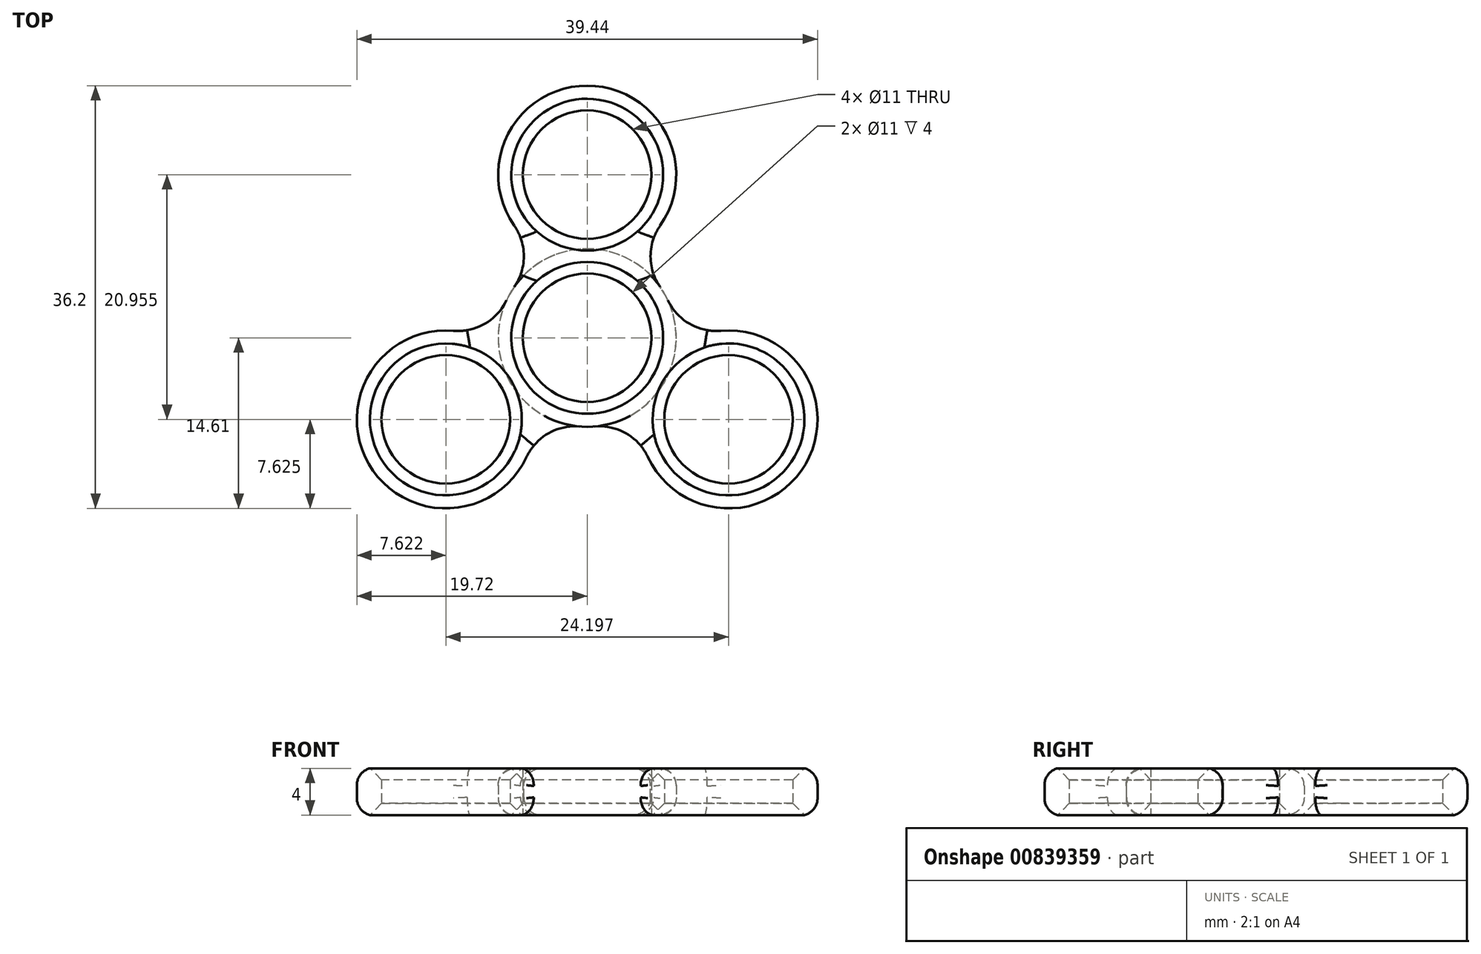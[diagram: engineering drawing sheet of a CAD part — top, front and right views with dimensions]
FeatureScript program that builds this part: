
annotation { "Feature Type Name" : "Feature", "Feature Type Description" : "" }
export const myFeature = defineFeature(function(context is Context, id is Id, definition is map)
    precondition{}
    {
        {
            var Q0;
            Q0=qCreatedBy(makeId("Top.planeOp"),FACE);
            var sketch = newSketch(context, id + "F0", { "sketchPlane" : qUnion([Q0])});
            skCircle(sketch, "E0", {"center": v(0, 0) * mm, "radius": 5.5 * mm});
            skCircle(sketch, "E1.cCircle", {"center": v(0, 13.97) * mm, "radius": 5.5 * mm});
            skCircle(sketch, "E2", {"center": v(0, 13.97) * mm, "radius": 7.62 * mm});
            skCircle(sketch, "E3", {"center": v(0, 0) * mm, "radius": 7.62 * mm});
            skSolve(sketch);
        }
        {
            var Q0;
            Q0=makeQuery(id+"F0.imprint","IMPRINT",FACE,{"disambiguationData":[TD([[makeQuery(id+"F0.imprint","IMPRINT",EDGE,{"derivedFrom":sQuery(id+"F0.wireOp",EDGE,"E0")}),-1.0]])]});
            var Q1;
            Q1=makeQuery(id+"F0.imprint","IMPRINT",FACE,{"disambiguationData":[TD([[makeQuery(id+"F0.imprint","IMPRINT",EDGE,{"derivedFrom":sQuery(id+"F0.wireOp",EDGE,"E1.cCircle")}),-1.0]])]});
            var Q2;
            {var subQ0=sQuery(id+"F0.wireOp",EDGE,"E3");var subQ1=sQuery(id+"F0.wireOp",EDGE,"E2");var subQ2=makeQuery(id+"F0.imprint","INTERSECT",VERTEX,{"disambiguationData":[OD(0.0)],"derivedFrom":[subQ1,subQ0]});Q2=makeQuery(id+"F0.imprint","IMPRINT",FACE,{"disambiguationData":[TD([[makeQuery(id+"F0.imprint","IMPRINT",EDGE,{"disambiguationData":[TD([[subQ2,-1.0]])],"derivedFrom":subQ1}),1.0]])]});}
            extrude(context, id + "F1", {"entities" : qUnion([Q0, Q1, Q2]), "depth" : 4 * mm, "offsetDistance" : 25.4 * mm});
        }
        {
            var Q0;
            {var subQ0=sQuery(id+"F0.wireOp",EDGE,"E3");var subQ1=sQuery(id+"F0.wireOp",EDGE,"E2");Q0=makeQuery(id+"F1.opExtrude","SWEPT_EDGE",EDGE,{"disambiguationData":[OSD([subQ1,subQ0]),TDD([makeQuery(id+"F0.imprint","INTERSECT",VERTEX,{"disambiguationData":[OD(0.0)],"derivedFrom":[subQ1,subQ0]})])]});}
            var Q1;
            {var subQ0=sQuery(id+"F0.wireOp",EDGE,"E3");var subQ1=sQuery(id+"F0.wireOp",EDGE,"E2");Q1=makeQuery(id+"F1.opExtrude","SWEPT_EDGE",EDGE,{"disambiguationData":[OSD([subQ1,subQ0]),TDD([makeQuery(id+"F0.imprint","INTERSECT",VERTEX,{"disambiguationData":[OD(1.0)],"derivedFrom":[subQ1,subQ0]})])]});}
            fillet(context, id + "F2", {"entities" : qUnion([Q0, Q1]), "radius" : 4.57 * mm, "tangentPropagation" : true, "allowEdgeOverflow" : false});
        }
        {
            var Q0;
            Q0=makeQuery(id+"F1.opExtrude","SWEPT_BODY",BODY,{"disambiguationData":[OSD([sQuery(id+"F0.wireOp",EDGE,"E0"),sQuery(id+"F0.wireOp",EDGE,"d1f96c89-ae24-44dc-95b8-3d53eee9b90a.0"),sQuery(id+"F0.wireOp",EDGE,"E1.0"),sQuery(id+"F0.wireOp",EDGE,"E1.1"),sQuery(id+"F0.wireOp",EDGE,"E1.2"),sQuery(id+"F0.wireOp",EDGE,"E1.3"),sQuery(id+"F0.wireOp",EDGE,"E1.4"),sQuery(id+"F0.wireOp",EDGE,"E1.5"),sQuery(id+"F0.wireOp",EDGE,"6467eb64-f5fc-4fa4-b67a-5fdd80484858.0"),sQuery(id+"F0.wireOp",EDGE,"6467eb64-f5fc-4fa4-b67a-5fdd80484858.2"),sQuery(id+"F0.wireOp",EDGE,"6467eb64-f5fc-4fa4-b67a-5fdd80484858.3"),sQuery(id+"F0.wireOp",EDGE,"6467eb64-f5fc-4fa4-b67a-5fdd80484858.4"),sQuery(id+"F0.wireOp",EDGE,"6467eb64-f5fc-4fa4-b67a-5fdd80484858.5"),sQuery(id+"F0.wireOp",EDGE,"e1e534cc-2f33-4b0f-82cc-b4de4e4070e7"),sQuery(id+"F0.wireOp",EDGE,"d04765f5-1735-495e-b364-6d969f9b3d5d"),sQuery(id+"F0.wireOp",EDGE,"77a682f6-1ae9-43b9-b4da-7f019d4a444a.0"),sQuery(id+"F0.wireOp",EDGE,"27ab2300-1543-4c0a-a06e-bdf80a921956.0"),sQuery(id+"F0.wireOp",EDGE,"7b8874fc-19ec-4d05-a443-a3cdac1f19cd.filletArc"),sQuery(id+"F0.wireOp",EDGE,"lxG7lnsp-9xvN-WL6z-RJoO-r6IwSvIQtlOm"),sQuery(id+"F0.wireOp",EDGE,"8nAJOfJ4-Ij3l-DfIw-Xt9b-HZkO6DjjanfU")])]});
            var Q1;
            Q1=makeQuery(id+"F1.opExtrude","SWEPT_FACE",FACE,{"disambiguationData":[OSD([sQuery(id+"F0.wireOp",EDGE,"E0")])]});
            circularPattern(context, id + "F3", {"entities" : qUnion([Q0]), "axis" : qUnion([Q1]), "angle" : 360 * degree, "instanceCount" : 3, "oppositeDirection" : true, "equalSpace" : true});
        }
        {
            var Q0;
            Q0=makeQuery(id+"F1.opExtrude","SWEPT_FACE",FACE,{"disambiguationData":[OSD([sQuery(id+"F0.wireOp",EDGE,"E0")])]});
            var Q1;
            Q1=makeQuery(id+"F3.opPattern","COPY",EDGE,{"derivedFrom":makeQuery(id+"F1.opExtrude","CAP_EDGE",EDGE,{"disambiguationData":[OSD([sQuery(id+"F0.wireOp",EDGE,"E1.3")])],"isStart":true}),"instanceName":"1"});
            var Q2;
            Q2=makeQuery(id+"F3.opPattern","COPY",EDGE,{"derivedFrom":makeQuery(id+"F1.opExtrude","CAP_EDGE",EDGE,{"disambiguationData":[OSD([sQuery(id+"F0.wireOp",EDGE,"E1.3")])],"isStart":false}),"instanceName":"1"});
            var Q3;
            Q3=makeQuery(id+"F3.opPattern","COPY",EDGE,{"derivedFrom":makeQuery(id+"F1.opExtrude","CAP_EDGE",EDGE,{"disambiguationData":[OSD([sQuery(id+"F0.wireOp",EDGE,"E1.2")])],"isStart":false}),"instanceName":"1"});
            var Q4;
            Q4=makeQuery(id+"F3.opPattern","COPY",EDGE,{"derivedFrom":makeQuery(id+"F1.opExtrude","CAP_EDGE",EDGE,{"disambiguationData":[OSD([sQuery(id+"F0.wireOp",EDGE,"E1.2")])],"isStart":true}),"instanceName":"1"});
            var Q5;
            Q5=makeQuery(id+"F3.opPattern","COPY",EDGE,{"derivedFrom":makeQuery(id+"F1.opExtrude","CAP_EDGE",EDGE,{"disambiguationData":[OSD([sQuery(id+"F0.wireOp",EDGE,"E1.1")])],"isStart":false}),"instanceName":"1"});
            var Q6;
            Q6=makeQuery(id+"F3.opPattern","COPY",EDGE,{"derivedFrom":makeQuery(id+"F1.opExtrude","CAP_EDGE",EDGE,{"disambiguationData":[OSD([sQuery(id+"F0.wireOp",EDGE,"E1.0")])],"isStart":false}),"instanceName":"1"});
            var Q7;
            Q7=makeQuery(id+"F3.opPattern","COPY",EDGE,{"derivedFrom":makeQuery(id+"F1.opExtrude","CAP_EDGE",EDGE,{"disambiguationData":[OSD([sQuery(id+"F0.wireOp",EDGE,"E1.5")])],"isStart":false}),"instanceName":"1"});
            var Q8;
            Q8=makeQuery(id+"F3.opPattern","COPY",EDGE,{"derivedFrom":makeQuery(id+"F1.opExtrude","CAP_EDGE",EDGE,{"disambiguationData":[OSD([sQuery(id+"F0.wireOp",EDGE,"E1.4")])],"isStart":true}),"instanceName":"1"});
            var Q9;
            Q9=makeQuery(id+"F3.opPattern","COPY",EDGE,{"derivedFrom":makeQuery(id+"F1.opExtrude","CAP_EDGE",EDGE,{"disambiguationData":[OSD([sQuery(id+"F0.wireOp",EDGE,"E1.4")])],"isStart":false}),"instanceName":"1"});
            var Q10;
            Q10=makeQuery(id+"F1.opExtrude","CAP_EDGE",EDGE,{"disambiguationData":[OSD([sQuery(id+"F0.wireOp",EDGE,"E1.1")])],"isStart":false});
            var Q11;
            Q11=makeQuery(id+"F1.opExtrude","CAP_EDGE",EDGE,{"disambiguationData":[OSD([sQuery(id+"F0.wireOp",EDGE,"E1.1")])],"isStart":true});
            var Q12;
            Q12=makeQuery(id+"F1.opExtrude","CAP_EDGE",EDGE,{"disambiguationData":[OSD([sQuery(id+"F0.wireOp",EDGE,"E1.0")])],"isStart":true});
            var Q13;
            Q13=makeQuery(id+"F1.opExtrude","CAP_EDGE",EDGE,{"disambiguationData":[OSD([sQuery(id+"F0.wireOp",EDGE,"E1.0")])],"isStart":false});
            var Q14;
            Q14=makeQuery(id+"F1.opExtrude","CAP_EDGE",EDGE,{"disambiguationData":[OSD([sQuery(id+"F0.wireOp",EDGE,"E1.5")])],"isStart":false});
            var Q15;
            Q15=makeQuery(id+"F1.opExtrude","CAP_EDGE",EDGE,{"disambiguationData":[OSD([sQuery(id+"F0.wireOp",EDGE,"E1.5")])],"isStart":true});
            var Q16;
            Q16=makeQuery(id+"F1.opExtrude","CAP_EDGE",EDGE,{"disambiguationData":[OSD([sQuery(id+"F0.wireOp",EDGE,"E1.4")])],"isStart":false});
            var Q17;
            Q17=makeQuery(id+"F1.opExtrude","CAP_EDGE",EDGE,{"disambiguationData":[OSD([sQuery(id+"F0.wireOp",EDGE,"E1.3")])],"isStart":false});
            var Q18;
            Q18=makeQuery(id+"F1.opExtrude","CAP_EDGE",EDGE,{"disambiguationData":[OSD([sQuery(id+"F0.wireOp",EDGE,"E1.2")])],"isStart":false});
            var Q19;
            Q19=makeQuery(id+"F1.opExtrude","CAP_EDGE",EDGE,{"disambiguationData":[OSD([sQuery(id+"F0.wireOp",EDGE,"E1.3")])],"isStart":true});
            var Q20;
            Q20=makeQuery(id+"F1.opExtrude","CAP_EDGE",EDGE,{"disambiguationData":[OSD([sQuery(id+"F0.wireOp",EDGE,"E1.4")])],"isStart":true});
            var Q21;
            Q21=makeQuery(id+"F1.opExtrude","CAP_EDGE",EDGE,{"disambiguationData":[OSD([sQuery(id+"F0.wireOp",EDGE,"E1.2")])],"isStart":true});
            var Q22;
            Q22=makeQuery(id+"F3.opPattern","COPY",EDGE,{"derivedFrom":makeQuery(id+"F1.opExtrude","CAP_EDGE",EDGE,{"disambiguationData":[OSD([sQuery(id+"F0.wireOp",EDGE,"E1.5")])],"isStart":true}),"instanceName":"1"});
            var Q23;
            Q23=makeQuery(id+"F3.opPattern","COPY",EDGE,{"derivedFrom":makeQuery(id+"F1.opExtrude","CAP_EDGE",EDGE,{"disambiguationData":[OSD([sQuery(id+"F0.wireOp",EDGE,"E1.0")])],"isStart":true}),"instanceName":"1"});
            var Q24;
            Q24=makeQuery(id+"F3.opPattern","COPY",EDGE,{"derivedFrom":makeQuery(id+"F1.opExtrude","CAP_EDGE",EDGE,{"disambiguationData":[OSD([sQuery(id+"F0.wireOp",EDGE,"E1.1")])],"isStart":true}),"instanceName":"1"});
            var Q25;
            Q25=makeQuery(id+"F3.opPattern","COPY",EDGE,{"derivedFrom":makeQuery(id+"F1.opExtrude","CAP_EDGE",EDGE,{"disambiguationData":[OSD([sQuery(id+"F0.wireOp",EDGE,"E1.5")])],"isStart":false}),"instanceName":"2"});
            var Q26;
            Q26=makeQuery(id+"F3.opPattern","COPY",EDGE,{"derivedFrom":makeQuery(id+"F1.opExtrude","CAP_EDGE",EDGE,{"disambiguationData":[OSD([sQuery(id+"F0.wireOp",EDGE,"E1.5")])],"isStart":true}),"instanceName":"2"});
            var Q27;
            Q27=makeQuery(id+"F3.opPattern","COPY",EDGE,{"derivedFrom":makeQuery(id+"F1.opExtrude","CAP_EDGE",EDGE,{"disambiguationData":[OSD([sQuery(id+"F0.wireOp",EDGE,"E1.0")])],"isStart":false}),"instanceName":"2"});
            var Q28;
            Q28=makeQuery(id+"F3.opPattern","COPY",EDGE,{"derivedFrom":makeQuery(id+"F1.opExtrude","CAP_EDGE",EDGE,{"disambiguationData":[OSD([sQuery(id+"F0.wireOp",EDGE,"E1.0")])],"isStart":true}),"instanceName":"2"});
            var Q29;
            Q29=makeQuery(id+"F3.opPattern","COPY",EDGE,{"derivedFrom":makeQuery(id+"F1.opExtrude","CAP_EDGE",EDGE,{"disambiguationData":[OSD([sQuery(id+"F0.wireOp",EDGE,"E1.4")])],"isStart":false}),"instanceName":"2"});
            var Q30;
            Q30=makeQuery(id+"F3.opPattern","COPY",EDGE,{"derivedFrom":makeQuery(id+"F1.opExtrude","CAP_EDGE",EDGE,{"disambiguationData":[OSD([sQuery(id+"F0.wireOp",EDGE,"E1.4")])],"isStart":true}),"instanceName":"2"});
            var Q31;
            Q31=makeQuery(id+"F3.opPattern","COPY",EDGE,{"derivedFrom":makeQuery(id+"F1.opExtrude","CAP_EDGE",EDGE,{"disambiguationData":[OSD([sQuery(id+"F0.wireOp",EDGE,"E1.3")])],"isStart":true}),"instanceName":"2"});
            var Q32;
            Q32=makeQuery(id+"F3.opPattern","COPY",EDGE,{"derivedFrom":makeQuery(id+"F1.opExtrude","CAP_EDGE",EDGE,{"disambiguationData":[OSD([sQuery(id+"F0.wireOp",EDGE,"E1.2")])],"isStart":true}),"instanceName":"2"});
            var Q33;
            Q33=makeQuery(id+"F3.opPattern","COPY",EDGE,{"derivedFrom":makeQuery(id+"F1.opExtrude","CAP_EDGE",EDGE,{"disambiguationData":[OSD([sQuery(id+"F0.wireOp",EDGE,"E1.1")])],"isStart":true}),"instanceName":"2"});
            var Q34;
            Q34=makeQuery(id+"F3.opPattern","COPY",EDGE,{"derivedFrom":makeQuery(id+"F1.opExtrude","CAP_EDGE",EDGE,{"disambiguationData":[OSD([sQuery(id+"F0.wireOp",EDGE,"E1.2")])],"isStart":false}),"instanceName":"2"});
            var Q35;
            Q35=makeQuery(id+"F3.opPattern","COPY",EDGE,{"derivedFrom":makeQuery(id+"F1.opExtrude","CAP_EDGE",EDGE,{"disambiguationData":[OSD([sQuery(id+"F0.wireOp",EDGE,"E1.1")])],"isStart":false}),"instanceName":"2"});
            var Q36;
            Q36=makeQuery(id+"F3.opPattern","COPY",EDGE,{"derivedFrom":makeQuery(id+"F1.opExtrude","CAP_EDGE",EDGE,{"disambiguationData":[OSD([sQuery(id+"F0.wireOp",EDGE,"E1.3")])],"isStart":false}),"instanceName":"2"});
            var Q37;
            Q37=makeQuery(id+"F3.opPattern","COPY",EDGE,{"derivedFrom":makeQuery(id+"F1.opExtrude","CAP_EDGE",EDGE,{"disambiguationData":[OSD([sQuery(id+"F0.wireOp",EDGE,"E1.5")])],"isStart":false}),"instanceName":"3"});
            var Q38;
            Q38=makeQuery(id+"F3.opPattern","COPY",EDGE,{"derivedFrom":makeQuery(id+"F1.opExtrude","CAP_EDGE",EDGE,{"disambiguationData":[OSD([sQuery(id+"F0.wireOp",EDGE,"E1.4")])],"isStart":false}),"instanceName":"3"});
            var Q39;
            Q39=makeQuery(id+"F3.opPattern","COPY",EDGE,{"derivedFrom":makeQuery(id+"F1.opExtrude","CAP_EDGE",EDGE,{"disambiguationData":[OSD([sQuery(id+"F0.wireOp",EDGE,"E1.3")])],"isStart":false}),"instanceName":"3"});
            var Q40;
            Q40=makeQuery(id+"F3.opPattern","COPY",EDGE,{"derivedFrom":makeQuery(id+"F1.opExtrude","CAP_EDGE",EDGE,{"disambiguationData":[OSD([sQuery(id+"F0.wireOp",EDGE,"E1.2")])],"isStart":false}),"instanceName":"3"});
            var Q41;
            Q41=makeQuery(id+"F3.opPattern","COPY",EDGE,{"derivedFrom":makeQuery(id+"F1.opExtrude","CAP_EDGE",EDGE,{"disambiguationData":[OSD([sQuery(id+"F0.wireOp",EDGE,"E1.1")])],"isStart":false}),"instanceName":"3"});
            var Q42;
            Q42=makeQuery(id+"F3.opPattern","COPY",EDGE,{"derivedFrom":makeQuery(id+"F1.opExtrude","CAP_EDGE",EDGE,{"disambiguationData":[OSD([sQuery(id+"F0.wireOp",EDGE,"E1.0")])],"isStart":false}),"instanceName":"3"});
            var Q43;
            Q43=makeQuery(id+"F3.opPattern","COPY",EDGE,{"derivedFrom":makeQuery(id+"F1.opExtrude","CAP_EDGE",EDGE,{"disambiguationData":[OSD([sQuery(id+"F0.wireOp",EDGE,"E1.5")])],"isStart":true}),"instanceName":"3"});
            var Q44;
            Q44=makeQuery(id+"F3.opPattern","COPY",EDGE,{"derivedFrom":makeQuery(id+"F1.opExtrude","CAP_EDGE",EDGE,{"disambiguationData":[OSD([sQuery(id+"F0.wireOp",EDGE,"E1.4")])],"isStart":true}),"instanceName":"3"});
            var Q45;
            Q45=makeQuery(id+"F3.opPattern","COPY",EDGE,{"derivedFrom":makeQuery(id+"F1.opExtrude","CAP_EDGE",EDGE,{"disambiguationData":[OSD([sQuery(id+"F0.wireOp",EDGE,"E1.3")])],"isStart":true}),"instanceName":"3"});
            var Q46;
            Q46=makeQuery(id+"F3.opPattern","COPY",EDGE,{"derivedFrom":makeQuery(id+"F1.opExtrude","CAP_EDGE",EDGE,{"disambiguationData":[OSD([sQuery(id+"F0.wireOp",EDGE,"E1.2")])],"isStart":true}),"instanceName":"3"});
            var Q47;
            Q47=makeQuery(id+"F3.opPattern","COPY",EDGE,{"derivedFrom":makeQuery(id+"F1.opExtrude","CAP_EDGE",EDGE,{"disambiguationData":[OSD([sQuery(id+"F0.wireOp",EDGE,"E1.1")])],"isStart":true}),"instanceName":"3"});
            var Q48;
            Q48=makeQuery(id+"F3.opPattern","COPY",EDGE,{"derivedFrom":makeQuery(id+"F1.opExtrude","CAP_EDGE",EDGE,{"disambiguationData":[OSD([sQuery(id+"F0.wireOp",EDGE,"E1.0")])],"isStart":true}),"instanceName":"3"});
            var Q49;
            Q49=makeQuery(id+"F3.opPattern","COPY",EDGE,{"derivedFrom":makeQuery(id+"F1.opExtrude","CAP_EDGE",EDGE,{"disambiguationData":[OSD([sQuery(id+"F0.wireOp",EDGE,"E1.cCircle")])],"isStart":false}),"instanceName":"2"});
            var Q50;
            Q50=makeQuery(id+"F1.opExtrude","CAP_EDGE",EDGE,{"disambiguationData":[OSD([sQuery(id+"F0.wireOp",EDGE,"E1.cCircle")])],"isStart":false});
            var Q51;
            Q51=makeQuery(id+"F3.opPattern","COPY",EDGE,{"derivedFrom":makeQuery(id+"F1.opExtrude","CAP_EDGE",EDGE,{"disambiguationData":[OSD([sQuery(id+"F0.wireOp",EDGE,"E1.cCircle")])],"isStart":false}),"instanceName":"1"});
            var Q52;
            Q52=makeQuery(id+"F3.opPattern","COPY",EDGE,{"derivedFrom":makeQuery(id+"F1.opExtrude","CAP_EDGE",EDGE,{"disambiguationData":[OSD([sQuery(id+"F0.wireOp",EDGE,"E1.cCircle")])],"isStart":true}),"instanceName":"1"});
            var Q53;
            Q53=makeQuery(id+"F1.opExtrude","CAP_EDGE",EDGE,{"disambiguationData":[OSD([sQuery(id+"F0.wireOp",EDGE,"E1.cCircle")])],"isStart":true});
            var Q54;
            Q54=makeQuery(id+"F3.opPattern","COPY",EDGE,{"derivedFrom":makeQuery(id+"F1.opExtrude","CAP_EDGE",EDGE,{"disambiguationData":[OSD([sQuery(id+"F0.wireOp",EDGE,"E1.cCircle")])],"isStart":true}),"instanceName":"2"});
            chamfer(context, id + "F4", {"entities" : qUnion([Q0, Q1, Q2, Q3, Q4, Q5, Q6, Q7, Q8, Q9, Q10, Q11, Q12, Q13, Q14, Q15, Q16, Q17, Q18, Q19, Q20, Q21, Q22, Q23, Q24, Q25, Q26, Q27, Q28, Q29, Q30, Q31, Q32, Q33, Q34, Q35, Q36, Q37, Q38, Q39, Q40, Q41, Q42, Q43, Q44, Q45, Q46, Q47, Q48, Q49, Q50, Q51, Q52, Q53, Q54]), "width" : 1 * mm, "tangentPropagation" : true});
        }
        {
            var Q0;
            Q0=makeQuery(id+"F1.opExtrude","CAP_EDGE",EDGE,{"disambiguationData":[OSD([sQuery(id+"F0.wireOp",EDGE,"E2")])],"isStart":false});
            var Q1;
            Q1=makeQuery(id+"F1.opExtrude","CAP_EDGE",EDGE,{"disambiguationData":[OSD([sQuery(id+"F0.wireOp",EDGE,"E2")])],"isStart":true});
            var Q2;
            Q2=makeQuery(id+"F3.opPattern","COPY",EDGE,{"derivedFrom":makeQuery(id+"F1.opExtrude","CAP_EDGE",EDGE,{"disambiguationData":[OSD([sQuery(id+"F0.wireOp",EDGE,"E2")])],"isStart":true}),"instanceName":"1"});
            var Q3;
            Q3=makeQuery(id+"F3.opPattern","COPY",EDGE,{"derivedFrom":makeQuery(id+"F1.opExtrude","CAP_EDGE",EDGE,{"disambiguationData":[OSD([sQuery(id+"F0.wireOp",EDGE,"E2")])],"isStart":false}),"instanceName":"1"});
            var Q4;
            Q4=makeQuery(id+"F3.opPattern","COPY",EDGE,{"derivedFrom":makeQuery(id+"F1.opExtrude","CAP_EDGE",EDGE,{"disambiguationData":[OSD([sQuery(id+"F0.wireOp",EDGE,"E2")])],"isStart":true}),"instanceName":"2"});
            var Q5;
            Q5=makeQuery(id+"F3.opPattern","COPY",EDGE,{"derivedFrom":makeQuery(id+"F1.opExtrude","CAP_EDGE",EDGE,{"disambiguationData":[OSD([sQuery(id+"F0.wireOp",EDGE,"E2")])],"isStart":false}),"instanceName":"2"});
            var Q6;
            Q6=makeQuery(id+"F3.opPattern","COPY",EDGE,{"derivedFrom":makeQuery(id+"F1.opExtrude","CAP_EDGE",EDGE,{"disambiguationData":[OSD([sQuery(id+"F0.wireOp",EDGE,"E2")])],"isStart":false}),"instanceName":"3"});
            var Q7;
            Q7=makeQuery(id+"F3.opPattern","COPY",EDGE,{"derivedFrom":makeQuery(id+"F1.opExtrude","CAP_EDGE",EDGE,{"disambiguationData":[OSD([sQuery(id+"F0.wireOp",EDGE,"E2")])],"isStart":true}),"instanceName":"3"});
            fillet(context, id + "F5", {"entities" : qUnion([Q0, Q1, Q2, Q3, Q4, Q5, Q6, Q7]), "radius" : 1.5 * mm, "tangentPropagation" : true, "allowEdgeOverflow" : false});
        }
    });
